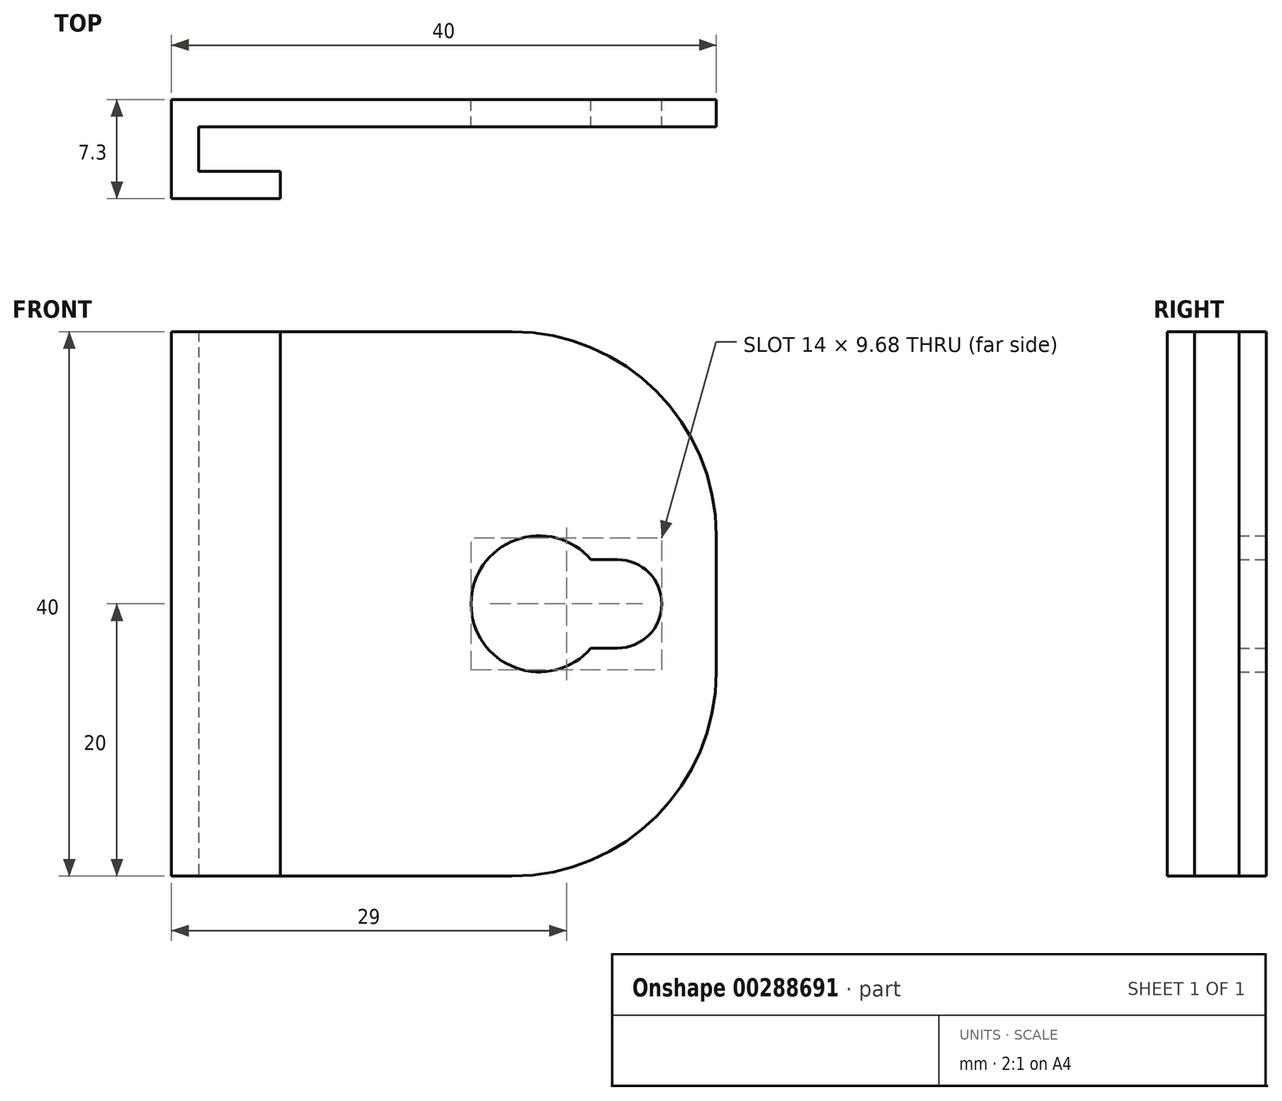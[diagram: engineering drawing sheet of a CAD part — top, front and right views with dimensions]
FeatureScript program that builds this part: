
annotation { "Feature Type Name" : "Feature", "Feature Type Description" : "" }
export const myFeature = defineFeature(function(context is Context, id is Id, definition is map)
    precondition{}
    {
        {
            var Q0;
            Q0=qCreatedBy(makeId("Top.planeOp"),FACE);
            var sketch = newSketch(context, id + "F0", { "sketchPlane" : qUnion([Q0])});
            skLineSegment(sketch, "E0.bottom", {"start": v(-12, -3.65) * mm, "end": v(-20, -3.65) * mm});
            skLineSegment(sketch, "E0.top", {"start": v(20, 3.65) * mm, "end": v(-20, 3.65) * mm});
            skLineSegment(sketch, "E0.right", {"start": v(-20, -3.65) * mm, "end": v(-20, 3.65) * mm});
            skPoint(sketch, "E0.middle", {"position": v(0, 0) * mm});
            skLineSegment(sketch, "E1.bottom", {"start": v(20, 1.65) * mm, "end": v(-18, 1.65) * mm});
            skLineSegment(sketch, "E1.top", {"start": v(-12, -1.65) * mm, "end": v(-18, -1.65) * mm});
            skLineSegment(sketch, "E1.right", {"start": v(-18, 1.65) * mm, "end": v(-18, -1.65) * mm});
            skLineSegment(sketch, "E2.trimOffspring", {"start": v(20, 1.65) * mm, "end": v(20, 3.65) * mm});
            skLineSegment(sketch, "E3", {"start": v(-18, 0) * mm, "end": v(-20, 0) * mm, "construction": true});
            skPoint(sketch, "E4.visualSharp", {"position": v(-18, 1.65) * mm});
            skLineSegment(sketch, "E5", {"start": v(-12, -1.65) * mm, "end": v(-12, -3.65) * mm});
            skSolve(sketch);
        }
        {
            var Q0;
            Q0=makeQuery(id+"F0.imprint","IMPRINT",FACE,{"disambiguationData":[TD([[makeQuery(id+"F0.imprint","IMPRINT",EDGE,{"derivedFrom":sQuery(id+"F0.wireOp",EDGE,"E0.bottom")}),-1.0]])]});
            extrude(context, id + "F1", {"entities" : qUnion([Q0]), "depth" : 40 * mm});
        }
        {
            var Q0;
            Q0=makeQuery(id+"F1.opExtrude","SWEPT_FACE",FACE,{"disambiguationData":[OSD([sQuery(id+"F0.wireOp",EDGE,"E0.top")])]});
            var sketch = newSketch(context, id + "F2", { "sketchPlane" : qUnion([Q0])});
            skArc(sketch, "E6", {"start": v(-10.8, 16.75) * mm, "mid": v(-2, 20) * mm, "end": v(-10.8, 23.25) * mm});
            skPoint(sketch, "E6.centerSnap0", {"position": v(-20, 20) * mm});
            skLineSegment(sketch, "E7.bottom", {"start": v(-7, 16.75) * mm, "end": v(-16, 16.75) * mm});
            skLineSegment(sketch, "E7.top", {"start": v(-7, 23.25) * mm, "end": v(-16, 23.25) * mm});
            skLineSegment(sketch, "E7.left", {"start": v(-7, 16.75) * mm, "end": v(-7, 23.25) * mm});
            skLineSegment(sketch, "E7.right", {"start": v(-16, 16.75) * mm, "end": v(-16, 23.25) * mm, "construction": true});
            skArc(sketch, "E8", {"start": v(-12.75, 23.25) * mm, "mid": v(-16, 20) * mm, "end": v(-12.75, 16.75) * mm});
            skPoint(sketch, "E8.centerSnap0", {"position": v(-16, 20) * mm});
            skSolve(sketch);
        }
        {
            var Q0;
            {var subQ4=sQuery(id+"F2.wireOp",EDGE,"E7.left");Q0=makeQuery(id+"F2.imprint","IMPRINT",FACE,{"disambiguationData":[TD([[makeQuery(id+"F2.imprint","IMPRINT",EDGE,{"derivedFrom":subQ4}),1.0]])]});}
            var Q1;
            {var subQ0=sQuery(id+"F2.wireOp",EDGE,"E6");Q1=makeQuery(id+"F2.imprint","IMPRINT",FACE,{"disambiguationData":[TD([[makeQuery(id+"F2.imprint","IMPRINT",EDGE,{"derivedFrom":subQ0}),1.0]])]});}
            extrude(context, id + "F3", {"entities" : qUnion([Q0, Q1]), "operationType" : NewBodyOperationType.REMOVE, "endBound" : BoundingType.UP_TO_NEXT, "oppositeDirection" : true, "depth" : 25 * mm});
        }
        {
            var Q0;
            Q0=makeQuery(id+"F1.opExtrude","CAP_EDGE",EDGE,{"disambiguationData":[OSD([sQuery(id+"F0.wireOp",EDGE,"E2.trimOffspring")])],"isStart":false});
            var Q1;
            Q1=makeQuery(id+"F1.opExtrude","CAP_EDGE",EDGE,{"disambiguationData":[OSD([sQuery(id+"F0.wireOp",EDGE,"E2.trimOffspring")])],"isStart":true});
            fillet(context, id + "F4", {"entities" : qUnion([Q0, Q1]), "radius" : 15 * mm, "tangentPropagation" : true, "allowEdgeOverflow" : false});
        }
    });
